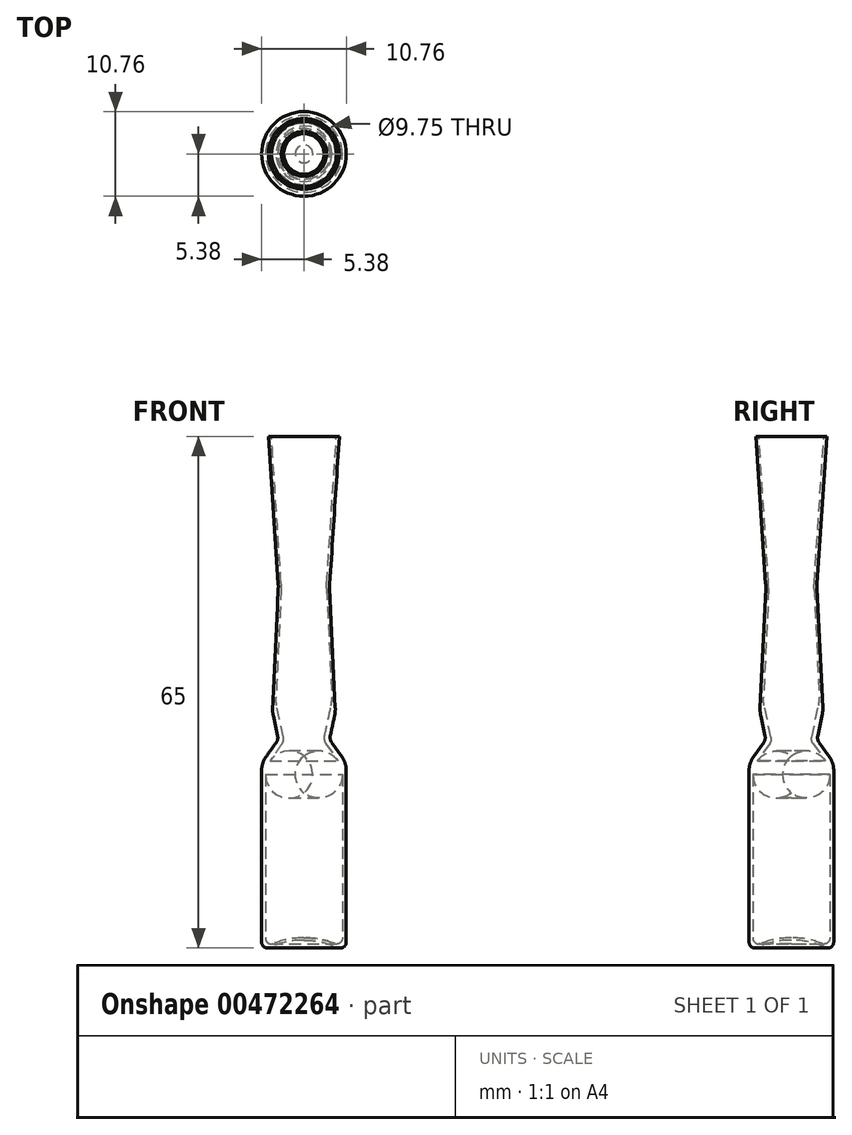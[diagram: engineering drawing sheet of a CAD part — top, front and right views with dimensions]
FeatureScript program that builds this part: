
annotation { "Feature Type Name" : "Feature", "Feature Type Description" : "" }
export const myFeature = defineFeature(function(context is Context, id is Id, definition is map)
    precondition{}
    {
        {
            var Q0;
            Q0=qCreatedBy(makeId("Front.planeOp"),FACE);
            var sketch = newSketch(context, id + "F0", { "sketchPlane" : qUnion([Q0])});
            skLineSegment(sketch, "E0", {"start": v(0, 0) * mm, "end": v(0, 82.71) * mm, "construction": true});
            skLineSegment(sketch, "E1", {"start": v(5.38, 0.75) * mm, "end": v(5.38, 23.5) * mm});
            skLineSegment(sketch, "E2", {"start": v(4.5, 65) * mm, "end": v(0, 65) * mm});
            skLineSegment(sketch, "E3", {"start": v(-6.37, 0) * mm, "end": v(4.63, 0) * mm, "construction": true});
            skArc(sketch, "E4", {"start": v(4.32, 0.07) * mm, "mid": v(5.03, 0.12) * mm, "end": v(5.38, 0.75) * mm});
            skArc(sketch, "E5", {"start": v(4.32, 0.07) * mm, "mid": v(2.2, 0.76) * mm, "end": v(0, 1) * mm});
            skLineSegment(sketch, "E6", {"start": v(-0.93, 1) * mm, "end": v(1.1, 1) * mm, "construction": true});
            skArc(sketch, "E7.0", {"start": v(3.92, 0.56) * mm, "mid": v(2, 1.11) * mm, "end": v(0, 1.3) * mm});
            skLineSegment(sketch, "E8.0", {"start": v(4.88, 1.21) * mm, "end": v(4.88, 23) * mm});
            skPoint(sketch, "E9.visualSharp", {"position": v(4.88, 0.13) * mm});
            skArc(sketch, "E9.filletArc", {"start": v(3.92, 0.56) * mm, "mid": v(4.57, 0.63) * mm, "end": v(4.88, 1.21) * mm});
            skLineSegment(sketch, "E10", {"start": v(0, 1.3) * mm, "end": v(0, 1) * mm});
            skLineSegment(sketch, "E11", {"start": v(5.38, 23.5) * mm, "end": v(3.25, 26.5) * mm});
            skLineSegment(sketch, "E12", {"start": v(3.25, 26.5) * mm, "end": v(4, 30) * mm});
            skLineSegment(sketch, "E13", {"start": v(4, 40.73) * mm, "end": v(4, 28.64) * mm, "construction": true});
            skLineSegment(sketch, "E14", {"start": v(3.25, 48.22) * mm, "end": v(3.25, 43.7) * mm, "construction": true});
            skLineSegment(sketch, "E15", {"start": v(-26.2, 46) * mm, "end": v(13, 46) * mm, "construction": true});
            skLineSegment(sketch, "E16", {"start": v(3.25, 23.02) * mm, "end": v(3.25, 32.34) * mm, "construction": true});
            skLineSegment(sketch, "E17", {"start": v(4, 30) * mm, "end": v(3.25, 45.96) * mm});
            skLineSegment(sketch, "E18", {"start": v(3.25, 45.96) * mm, "end": v(4.5, 65) * mm});
            skLineSegment(sketch, "E19.0", {"start": v(2.5, 26.35) * mm, "end": v(3.57, 31.32) * mm});
            skLineSegment(sketch, "E19.1", {"start": v(4.88, 23) * mm, "end": v(2.5, 26.35) * mm});
            skLineSegment(sketch, "E20.0", {"start": v(2.88, 45.97) * mm, "end": v(4.13, 65.02) * mm});
            skLineSegment(sketch, "E20.1", {"start": v(3.57, 31.32) * mm, "end": v(2.88, 45.97) * mm});
            skSolve(sketch);
        }
        {
            var Q0;
            Q0=qSketchRegion(id+"F0",true);
            var Q1;
            Q1=sQuery(id+"F0.wireOp",EDGE,"E0");
            revolve(context, id + "F1", {"entities" : qUnion([Q0]), "axis" : qUnion([Q1]), "revolveType" : RevolveType.FULL});
        }
        {
            var Q0;
            Q0=makeQuery(id+"F1.opRevolve","SWEPT_EDGE",EDGE,{"disambiguationData":[OSD([sQuery(id+"F0.wireOp",EDGE,"E1"),sQuery(id+"F0.wireOp",EDGE,"E11")])]});
            var Q1;
            Q1=makeQuery(id+"F1.opRevolve","SWEPT_EDGE",EDGE,{"disambiguationData":[OSD([sQuery(id+"F0.wireOp",EDGE,"E8.0"),sQuery(id+"F0.wireOp",EDGE,"E19.1")])]});
            fillet(context, id + "F2", {"entities" : qUnion([Q0, Q1]), "radius" : 3 * mm, "tangentPropagation" : true, "allowEdgeOverflow" : false});
        }
        {
            var Q0;
            Q0=makeQuery(id+"F1.opRevolve","SWEPT_EDGE",EDGE,{"disambiguationData":[OSD([sQuery(id+"F0.wireOp",EDGE,"E11"),sQuery(id+"F0.wireOp",EDGE,"E12")])]});
            var Q1;
            Q1=makeQuery(id+"F1.opRevolve","SWEPT_EDGE",EDGE,{"disambiguationData":[OSD([sQuery(id+"F0.wireOp",EDGE,"E19.0"),sQuery(id+"F0.wireOp",EDGE,"E19.1")])]});
            fillet(context, id + "F3", {"entities" : qUnion([Q0, Q1]), "radius" : 1 * mm, "tangentPropagation" : true, "allowEdgeOverflow" : false});
        }
        {
            var Q0;
            Q0=makeQuery(id+"F1.opRevolve","SWEPT_EDGE",EDGE,{"disambiguationData":[OSD([sQuery(id+"F0.wireOp",EDGE,"E12"),sQuery(id+"F0.wireOp",EDGE,"E17")])]});
            var Q1;
            Q1=makeQuery(id+"F1.opRevolve","SWEPT_EDGE",EDGE,{"disambiguationData":[OSD([sQuery(id+"F0.wireOp",EDGE,"E19.0"),sQuery(id+"F0.wireOp",EDGE,"E20.1")])]});
            fillet(context, id + "F4", {"entities" : qUnion([Q0, Q1]), "radius" : 4 * mm, "tangentPropagation" : true, "allowEdgeOverflow" : false});
        }
        {
            var Q0;
            Q0=makeQuery(id+"F1.opRevolve","SWEPT_EDGE",EDGE,{"disambiguationData":[OSD([sQuery(id+"F0.wireOp",EDGE,"E17"),sQuery(id+"F0.wireOp",EDGE,"E18")])]});
            var Q1;
            Q1=makeQuery(id+"F1.opRevolve","SWEPT_EDGE",EDGE,{"disambiguationData":[OSD([sQuery(id+"F0.wireOp",EDGE,"E20.0"),sQuery(id+"F0.wireOp",EDGE,"E20.1")])]});
            fillet(context, id + "F5", {"entities" : qUnion([Q0, Q1]), "radius" : 5 * mm, "tangentPropagation" : true, "allowEdgeOverflow" : false});
        }
    });
